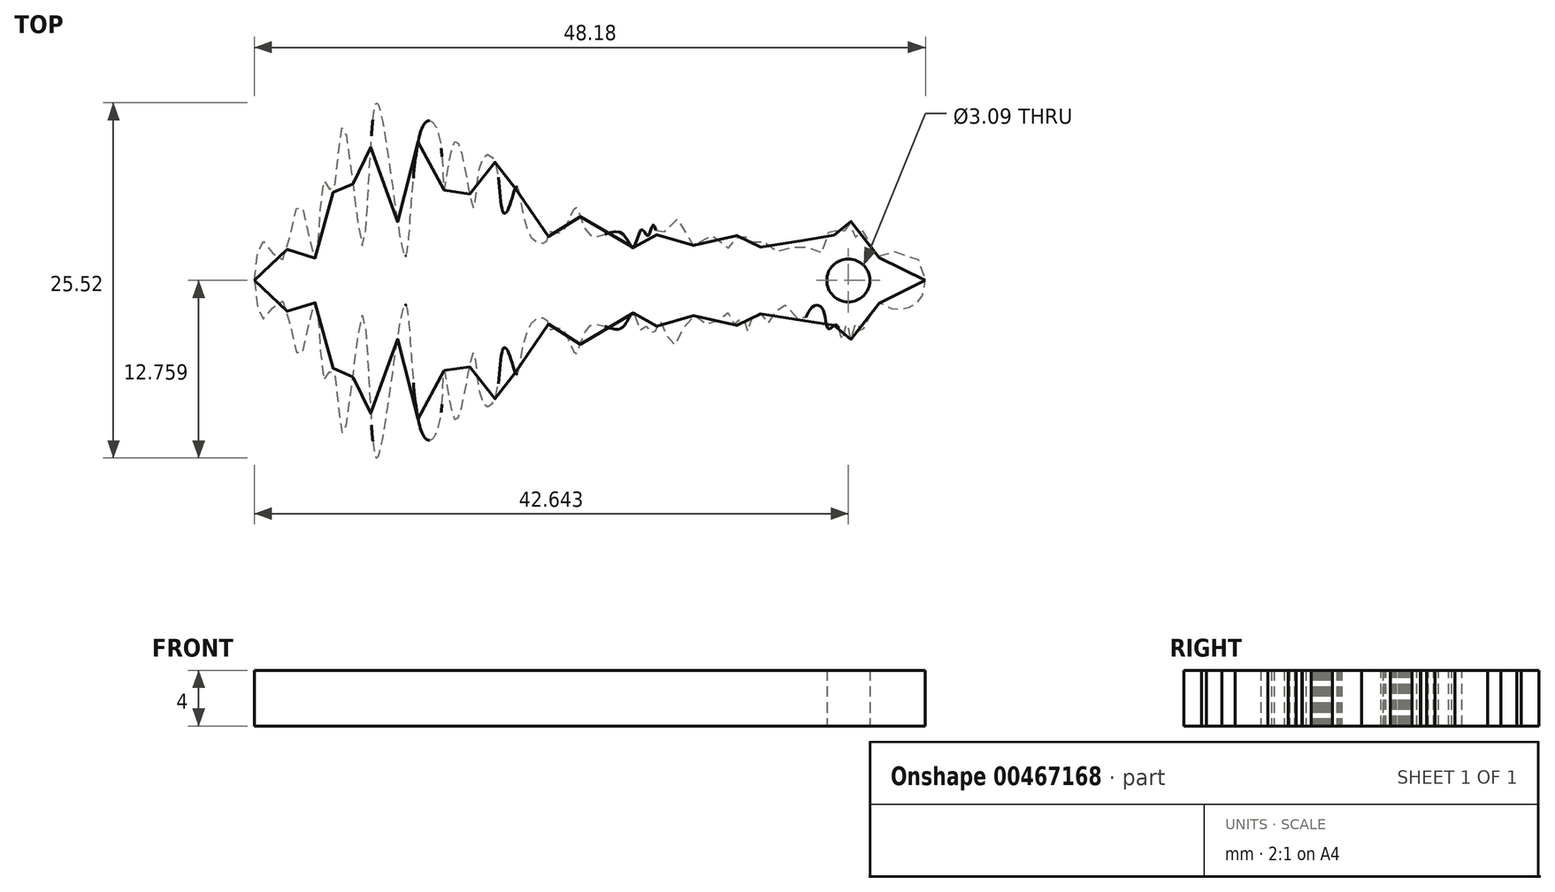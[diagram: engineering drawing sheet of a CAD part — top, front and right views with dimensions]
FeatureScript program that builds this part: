
annotation { "Feature Type Name" : "Feature", "Feature Type Description" : "" }
export const myFeature = defineFeature(function(context is Context, id is Id, definition is map)
    precondition{}
    {
        {
            var Q0;
            Q0=qCreatedBy(makeId("Top.planeOp"),FACE);
            var sketch = newSketch(context, id + "F0", { "sketchPlane" : qUnion([Q0])});
            skLineSegment(sketch, "E0", {"start": v(-31.23, -6.72) * mm, "end": v(16.95, -6.72) * mm});
            skFitSpline(sketch, "E1", {"points": [v(-31.23, -6.72) * mm, v(-30.51, -3.96) * mm, v(-29.3, -5.29) * mm, v(-28, -1.18) * mm, v(-26.87, -5.12) * mm, v(-26.17, 0.5) * mm, v(-25.64, -0.45) * mm, v(-24.86, 4.42) * mm, v(-23.44, -4.27) * mm, v(-22.47, 6.03) * mm, v(-20.43, -4.96) * mm, v(-19.1, 4.45) * mm, v(-18.12, 4.14) * mm, v(-17.6, -0.23) * mm, v(-16.76, 3.3) * mm, v(-15.5, -1.54) * mm, v(-14.8, 2.1) * mm, v(-14.03, 1.94) * mm, v(-13.36, -1.84) * mm, v(-13.03, -1.65) * mm, v(-12.39, 0) * mm, v(-11.33, -3.65) * mm, v(-10.22, -3.85) * mm, v(-10.02, -3.18) * mm, v(-9.21, -3.3) * mm, v(-8.16, -1.46) * mm, v(-7.1, -3.49) * mm, v(-4.93, -3.26) * mm, v(-4.04, -4.38) * mm, v(-3.42, -3.07) * mm, v(-2.98, -3.52) * mm, v(-2.59, -2.74) * mm, v(-2.11, -3.85) * mm, v(-1.2, -2.04) * mm, v(0.22, -4.18) * mm, v(1.53, -3.48) * mm, v(2.75, -4.42) * mm, v(3.34, -3.46) * mm, v(3.8, -4.19) * mm, v(4.17, -3.07) * mm, v(4.82, -4.54) * mm, v(5.68, -3.66) * mm, v(6.63, -5.03) * mm, v(8, -3.83) * mm, v(8.81, -4.8) * mm, v(9.54, -4.7) * mm, v(10.01, -3.24) * mm, v(10.58, -3.52) * mm, v(10.96, -2.45) * mm, v(11.31, -3.6) * mm, v(11.59, -2.47) * mm, v(11.98, -3.71) * mm, v(12.3, -3.1) * mm, v(13.54, -5.03) * mm, v(14.48, -4.72) * mm, v(16.41, -5.2) * mm, v(16.95, -6.72) * mm], "startDerivative": vector(21.91, 219.25) * mm, "endDerivative": vector(11.6, -108.83) * mm});
            skFitSpline(sketch, "E2.MirrorCS", {"points": [v(-31.23, -6.72) * mm, v(-30.51, -9.48) * mm, v(-29.3, -8.15) * mm, v(-28, -12.27) * mm, v(-26.87, -8.33) * mm, v(-26.17, -13.94) * mm, v(-25.64, -12.99) * mm, v(-24.86, -17.86) * mm, v(-23.44, -9.17) * mm, v(-22.47, -19.48) * mm, v(-20.43, -8.48) * mm, v(-19.1, -17.89) * mm, v(-18.12, -17.58) * mm, v(-17.6, -13.21) * mm, v(-16.76, -16.75) * mm, v(-15.5, -11.9) * mm, v(-14.8, -15.55) * mm, v(-14.03, -15.38) * mm, v(-13.36, -11.6) * mm, v(-13.03, -11.8) * mm, v(-12.39, -13.44) * mm, v(-11.33, -9.79) * mm, v(-10.22, -9.6) * mm, v(-10.02, -10.26) * mm, v(-9.21, -10.15) * mm, v(-8.16, -11.99) * mm, v(-7.1, -9.95) * mm, v(-4.93, -10.18) * mm, v(-4.04, -9.06) * mm, v(-3.42, -10.37) * mm, v(-2.98, -9.93) * mm, v(-2.59, -10.7) * mm, v(-2.11, -9.6) * mm, v(-1.2, -11.4) * mm, v(0.22, -9.26) * mm, v(1.53, -9.96) * mm, v(2.75, -9.02) * mm, v(3.34, -9.98) * mm, v(3.8, -9.25) * mm, v(4.17, -10.38) * mm, v(4.82, -8.9) * mm, v(5.68, -9.79) * mm, v(6.63, -8.4) * mm, v(8, -9.6) * mm, v(8.81, -8.64) * mm, v(9.54, -8.74) * mm, v(10.01, -10.2) * mm, v(10.58, -9.92) * mm, v(10.96, -10.99) * mm, v(11.31, -9.85) * mm, v(11.59, -10.97) * mm, v(11.98, -9.73) * mm, v(12.3, -10.34) * mm, v(13.54, -8.4) * mm, v(14.48, -8.72) * mm, v(16.41, -8.25) * mm, v(16.95, -6.72) * mm], "startDerivative": vector(21.91, -219.25) * mm, "endDerivative": vector(11.6, 108.83) * mm});
            skCircle(sketch, "E3", {"center": v(11.41, -6.72) * mm, "radius": 1.54 * mm});
            skSolve(sketch);
        }
        {
            var Q0;
            {var subQ0=sQuery(id+"F0.wireOp",EDGE,"E2.MirrorCS");Q0=makeQuery(id+"F0.imprint","IMPRINT",FACE,{"disambiguationData":[TD([[makeQuery(id+"F0.imprint","IMPRINT",EDGE,{"derivedFrom":subQ0}),1.0]])]});}
            var Q1;
            {var subQ1=sQuery(id+"F0.wireOp",EDGE,"E1");Q1=makeQuery(id+"F0.imprint","IMPRINT",FACE,{"disambiguationData":[TD([[makeQuery(id+"F0.imprint","IMPRINT",EDGE,{"derivedFrom":subQ1}),-1.0]])]});}
            extrude(context, id + "F1", {"entities" : qUnion([Q0, Q1]), "depth" : 4 * mm});
        }
    });
